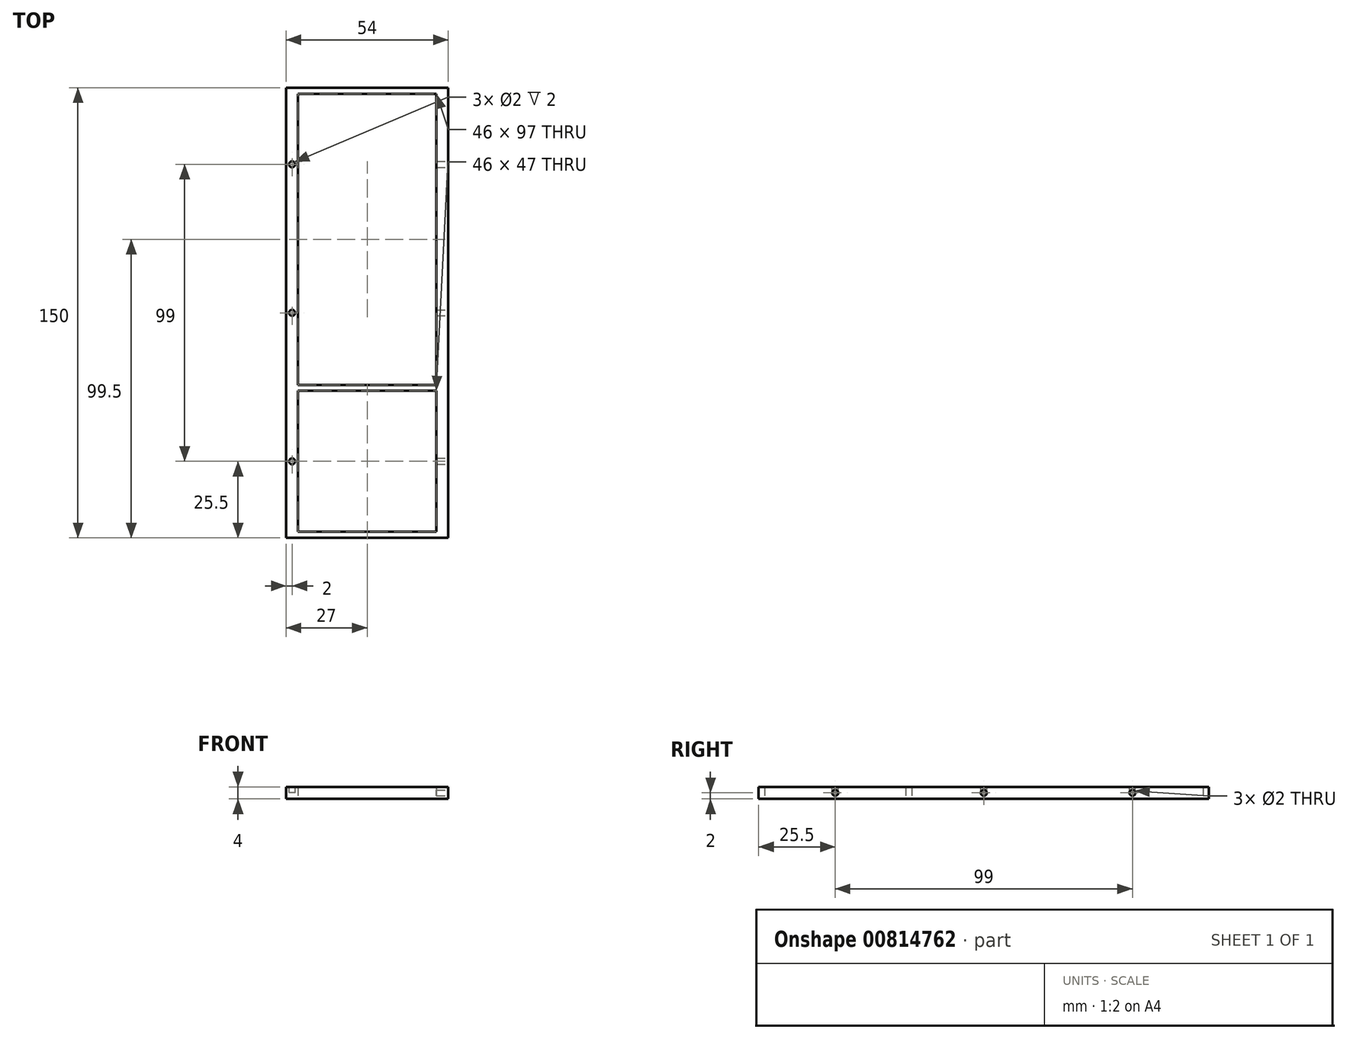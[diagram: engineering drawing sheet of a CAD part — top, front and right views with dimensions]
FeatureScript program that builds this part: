
annotation { "Feature Type Name" : "Feature", "Feature Type Description" : "" }
export const myFeature = defineFeature(function(context is Context, id is Id, definition is map)
    precondition{}
    {
        {
            var Q0;
            Q0=qCreatedBy(makeId("Top.planeOp"),FACE);
            var sketch = newSketch(context, id + "F0", { "sketchPlane" : qUnion([Q0])});
            skLineSegment(sketch, "E0.bottom", {"start": v(-27, 75) * mm, "end": v(27, 75) * mm});
            skLineSegment(sketch, "E0.top", {"start": v(-27, -75) * mm, "end": v(27, -75) * mm});
            skLineSegment(sketch, "E0.left", {"start": v(-27, 75) * mm, "end": v(-27, -75) * mm});
            skLineSegment(sketch, "E0.right", {"start": v(27, 75) * mm, "end": v(27, -75) * mm});
            skPoint(sketch, "E0.middle", {"position": v(0, 0) * mm});
            skLineSegment(sketch, "E1.bottom", {"start": v(-23, -26) * mm, "end": v(23, -26) * mm});
            skLineSegment(sketch, "E1.top", {"start": v(-23, -73) * mm, "end": v(23, -73) * mm});
            skLineSegment(sketch, "E1.left", {"start": v(-23, -26) * mm, "end": v(-23, -73) * mm});
            skLineSegment(sketch, "E1.right", {"start": v(23, -26) * mm, "end": v(23, -73) * mm});
            skPoint(sketch, "E1.middle", {"position": v(0, -49.5) * mm});
            skLineSegment(sketch, "E2.bottom", {"start": v(-23, 73) * mm, "end": v(23, 73) * mm});
            skLineSegment(sketch, "E2.top", {"start": v(-23, -24) * mm, "end": v(23, -24) * mm});
            skLineSegment(sketch, "E2.left", {"start": v(-23, 73) * mm, "end": v(-23, -24) * mm});
            skLineSegment(sketch, "E2.right", {"start": v(23, 73) * mm, "end": v(23, -24) * mm});
            skPoint(sketch, "E2.middle", {"position": v(0, 24.5) * mm});
            skSolve(sketch);
        }
        {
            var Q0;
            Q0=qSketchRegion(id+"F0",true);
            extrude(context, id + "F1", {"entities" : qUnion([Q0]), "depth" : 4 * mm, "offsetDistance" : 25 * mm});
        }
        {
            var Q0;
            Q0=makeQuery(id+"F1.opExtrude","SWEPT_FACE",FACE,{"disambiguationData":[OSD([sQuery(id+"F0.wireOp",EDGE,"E0.right")])]});
            var sketch = newSketch(context, id + "F2", { "sketchPlane" : qUnion([Q0])});
            skPoint(sketch, "E3", {"position": v(-49.5, 2) * mm});
            skLineSegment(sketch, "E4", {"start": v(-24, 4) * mm, "end": v(-24, 0) * mm});
            skPoint(sketch, "E5", {"position": v(0, 2) * mm});
            skPoint(sketch, "E6", {"position": v(49.5, 2) * mm});
            skCircle(sketch, "E7", {"center": v(-49.5, 2) * mm, "radius": 1 * mm});
            skCircle(sketch, "E8", {"center": v(0, 2) * mm, "radius": 1 * mm});
            skCircle(sketch, "E9", {"center": v(49.5, 2) * mm, "radius": 1 * mm});
            skSolve(sketch);
        }
        {
            var Q0;
            Q0=qSketchRegion(id+"F2",true);
            extrude(context, id + "F3", {"entities" : qUnion([Q0]), "operationType" : NewBodyOperationType.REMOVE, "oppositeDirection" : true, "depth" : 25 * mm, "offsetDistance" : 25 * mm});
        }
        {
            var Q0;
            Q0=makeQuery(id+"F1.opExtrude","CAP_FACE",FACE,{"disambiguationData":[OSD([sQuery(id+"F0.wireOp",EDGE,"E0.bottom"),sQuery(id+"F0.wireOp",EDGE,"E0.top"),sQuery(id+"F0.wireOp",EDGE,"E0.left"),sQuery(id+"F0.wireOp",EDGE,"E0.right"),sQuery(id+"F0.wireOp",EDGE,"E1.bottom"),sQuery(id+"F0.wireOp",EDGE,"E1.top"),sQuery(id+"F0.wireOp",EDGE,"E1.left"),sQuery(id+"F0.wireOp",EDGE,"E1.right"),sQuery(id+"F0.wireOp",EDGE,"E2.bottom"),sQuery(id+"F0.wireOp",EDGE,"E2.top"),sQuery(id+"F0.wireOp",EDGE,"E2.left"),sQuery(id+"F0.wireOp",EDGE,"E2.right")])],"isStart":false});
            var sketch = newSketch(context, id + "F4", { "sketchPlane" : qUnion([Q0])});
            skCircle(sketch, "E10", {"center": v(-25, -49.5) * mm, "radius": 1 * mm});
            skCircle(sketch, "E11", {"center": v(-25, 0) * mm, "radius": 1 * mm});
            skCircle(sketch, "E12", {"center": v(-25, 49.5) * mm, "radius": 1 * mm});
            skLineSegment(sketch, "E13", {"start": v(-23, -24) * mm, "end": v(-27, -24) * mm});
            skSolve(sketch);
        }
        {
            var Q0;
            Q0=qSketchRegion(id+"F4",true);
            extrude(context, id + "F5", {"entities" : qUnion([Q0]), "operationType" : NewBodyOperationType.REMOVE, "oppositeDirection" : true, "depth" : 2 * mm, "offsetDistance" : 25 * mm});
        }
    });
